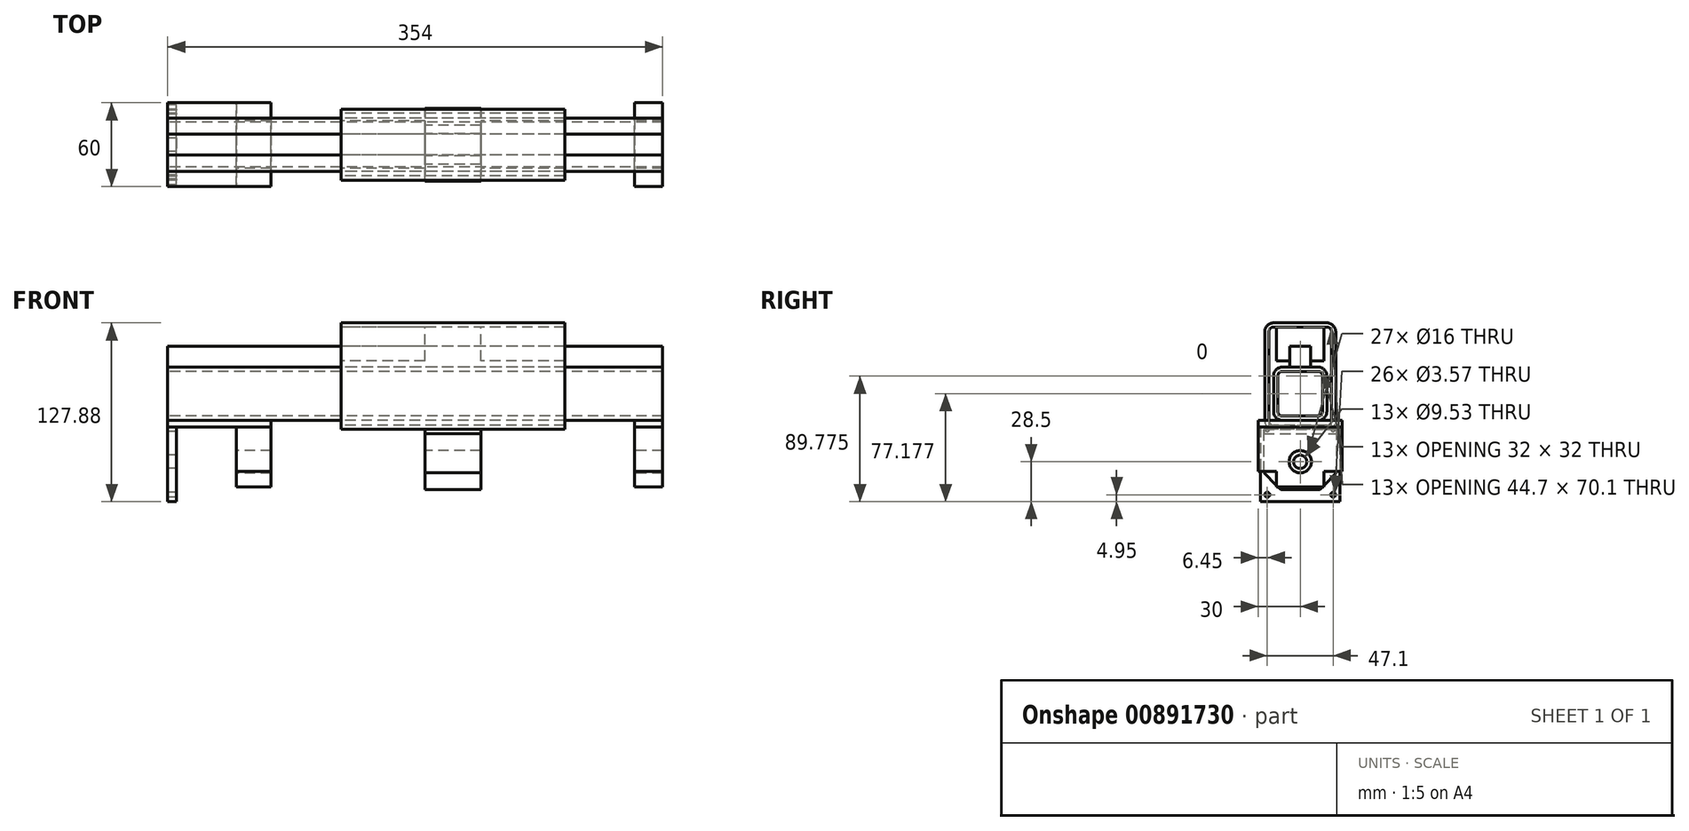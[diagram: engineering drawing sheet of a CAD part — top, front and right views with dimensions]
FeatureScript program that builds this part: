
annotation { "Feature Type Name" : "Feature", "Feature Type Description" : "" }
export const myFeature = defineFeature(function(context is Context, id is Id, definition is map)
    precondition{}
    {
        {
            var Q0;
            Q0=qCreatedBy(makeId("Right.planeOp"),FACE);
            var sketch = newSketch(context, id + "F0", { "sketchPlane" : qUnion([Q0])});
            skLineSegment(sketch, "E0", {"start": v(-26, 20) * mm, "end": v(26, 20) * mm});
            skLineSegment(sketch, "E1", {"start": v(26, 20) * mm, "end": v(26, -7.98) * mm});
            skLineSegment(sketch, "E2", {"start": v(26, -7.98) * mm, "end": v(13.98, -20) * mm});
            skLineSegment(sketch, "E3", {"start": v(13.98, -20) * mm, "end": v(-13.98, -20) * mm});
            skLineSegment(sketch, "E4", {"start": v(-13.98, -20) * mm, "end": v(-26, -7.98) * mm});
            skLineSegment(sketch, "E5", {"start": v(-26, -7.98) * mm, "end": v(-26, 20) * mm});
            skPoint(sketch, "E6", {"position": v(0, 0) * mm});
            skCircle(sketch, "E7", {"center": v(0, 0) * mm, "radius": 8 * mm});
            skSolve(sketch);
        }
        {
            var Q0;
            Q0=qCreatedBy(makeId("Right.planeOp"),FACE);
            var sketch = newSketch(context, id + "F1", { "sketchPlane" : qUnion([Q0])});
            skLineSegment(sketch, "E8.bottom", {"start": v(19.18, 96.33) * mm, "end": v(-19.18, 96.33) * mm});
            skLineSegment(sketch, "E8.top", {"start": v(19.18, 26.22) * mm, "end": v(-19.18, 26.22) * mm});
            skLineSegment(sketch, "E8.left", {"start": v(22.35, 93.15) * mm, "end": v(22.35, 29.4) * mm});
            skLineSegment(sketch, "E8.right", {"start": v(-22.35, 93.15) * mm, "end": v(-22.35, 29.4) * mm});
            skPoint(sketch, "E8.middle", {"position": v(0, 61.28) * mm});
            skLineSegment(sketch, "E9.bottom", {"start": v(19.05, 99.38) * mm, "end": v(-19.05, 99.38) * mm});
            skLineSegment(sketch, "E9.top", {"start": v(19.05, 23.18) * mm, "end": v(-19.05, 23.18) * mm});
            skLineSegment(sketch, "E9.left", {"start": v(25.4, 93.03) * mm, "end": v(25.4, 29.53) * mm});
            skLineSegment(sketch, "E9.right", {"start": v(-25.4, 93.03) * mm, "end": v(-25.4, 29.53) * mm});
            skPoint(sketch, "E10.visualSharp", {"position": v(-22.35, 96.33) * mm});
            skArc(sketch, "E10.filletArc", {"start": v(-19.18, 96.33) * mm, "mid": v(-21.42, 95.4) * mm, "end": v(-22.35, 93.15) * mm});
            skPoint(sketch, "E11.visualSharp", {"position": v(22.35, 96.33) * mm});
            skArc(sketch, "E11.filletArc", {"start": v(22.35, 93.15) * mm, "mid": v(21.42, 95.4) * mm, "end": v(19.18, 96.33) * mm});
            skPoint(sketch, "E12.visualSharp", {"position": v(22.35, 26.22) * mm});
            skArc(sketch, "E12.filletArc", {"start": v(19.18, 26.22) * mm, "mid": v(21.42, 27.15) * mm, "end": v(22.35, 29.4) * mm});
            skPoint(sketch, "E13.visualSharp", {"position": v(-22.35, 26.22) * mm});
            skArc(sketch, "E13.filletArc", {"start": v(-22.35, 29.4) * mm, "mid": v(-21.42, 27.15) * mm, "end": v(-19.18, 26.22) * mm});
            skPoint(sketch, "E14.visualSharp", {"position": v(-25.4, 99.38) * mm});
            skArc(sketch, "E14.filletArc", {"start": v(-19.05, 99.38) * mm, "mid": v(-23.54, 97.52) * mm, "end": v(-25.4, 93.03) * mm});
            skPoint(sketch, "E15.visualSharp", {"position": v(25.4, 99.38) * mm});
            skArc(sketch, "E15.filletArc", {"start": v(25.4, 93.03) * mm, "mid": v(23.54, 97.52) * mm, "end": v(19.05, 99.38) * mm});
            skPoint(sketch, "E16.visualSharp", {"position": v(25.4, 23.18) * mm});
            skArc(sketch, "E16.filletArc", {"start": v(19.05, 23.18) * mm, "mid": v(23.54, 25.03) * mm, "end": v(25.4, 29.53) * mm});
            skPoint(sketch, "E17.visualSharp", {"position": v(-25.4, 23.18) * mm});
            skArc(sketch, "E17.filletArc", {"start": v(-25.4, 29.53) * mm, "mid": v(-23.54, 25.03) * mm, "end": v(-19.05, 23.18) * mm});
            skLineSegment(sketch, "E18.bottom", {"start": v(-26, 23.18) * mm, "end": v(26, 23.18) * mm});
            skLineSegment(sketch, "E18.top", {"start": v(-26, 20) * mm, "end": v(26, 20) * mm});
            skLineSegment(sketch, "E18.left", {"start": v(-26, 23.18) * mm, "end": v(-26, 20) * mm});
            skLineSegment(sketch, "E18.right", {"start": v(26, 23.18) * mm, "end": v(26, 20) * mm});
            skSolve(sketch);
        }
        {
            var Q0;
            Q0=qCreatedBy(makeId("Right.planeOp"),FACE);
            var sketch = newSketch(context, id + "F2", { "sketchPlane" : qUnion([Q0])});
            skLineSegment(sketch, "E19.bottom", {"start": v(7.5, 67.73) * mm, "end": v(-7.5, 67.73) * mm});
            skLineSegment(sketch, "E19.top", {"start": v(7.5, 82.73) * mm, "end": v(-7.5, 82.73) * mm});
            skLineSegment(sketch, "E19.left", {"start": v(7.5, 67.73) * mm, "end": v(7.5, 82.73) * mm});
            skLineSegment(sketch, "E19.right", {"start": v(-7.5, 67.73) * mm, "end": v(-7.5, 82.73) * mm});
            skPoint(sketch, "E19.middle", {"position": v(0, 75.23) * mm});
            skLineSegment(sketch, "E20.bottom", {"start": v(17, 72.33) * mm, "end": v(-17, 72.33) * mm});
            skLineSegment(sketch, "E20.top", {"start": v(17, 96.33) * mm, "end": v(-17, 96.33) * mm});
            skLineSegment(sketch, "E20.left", {"start": v(17, 72.33) * mm, "end": v(17, 96.33) * mm});
            skLineSegment(sketch, "E20.right", {"start": v(-17, 72.33) * mm, "end": v(-17, 96.33) * mm});
            skPoint(sketch, "E20.middle", {"position": v(0, 84.33) * mm});
            skSolve(sketch);
        }
        {
            var Q0;
            Q0=qCreatedBy(makeId("Right.planeOp"),FACE);
            var sketch = newSketch(context, id + "F3", { "sketchPlane" : qUnion([Q0])});
            skLineSegment(sketch, "E21.bottom", {"start": v(12.83, 64.68) * mm, "end": v(-12.83, 64.68) * mm});
            skLineSegment(sketch, "E21.top", {"start": v(12.83, 32.67) * mm, "end": v(-12.83, 32.67) * mm});
            skLineSegment(sketch, "E21.left", {"start": v(16, 61.5) * mm, "end": v(16, 35.85) * mm});
            skLineSegment(sketch, "E21.right", {"start": v(-16, 61.5) * mm, "end": v(-16, 35.85) * mm});
            skPoint(sketch, "E21.middle", {"position": v(0, 48.68) * mm});
            skLineSegment(sketch, "E22.bottom", {"start": v(12.7, 67.73) * mm, "end": v(-12.7, 67.73) * mm});
            skLineSegment(sketch, "E22.top", {"start": v(12.7, 29.63) * mm, "end": v(-12.7, 29.63) * mm});
            skLineSegment(sketch, "E22.left", {"start": v(19.05, 61.38) * mm, "end": v(19.05, 35.98) * mm});
            skLineSegment(sketch, "E22.right", {"start": v(-19.05, 61.38) * mm, "end": v(-19.05, 35.98) * mm});
            skPoint(sketch, "E23.visualSharp", {"position": v(-16, 64.68) * mm});
            skArc(sketch, "E23.filletArc", {"start": v(-12.83, 64.68) * mm, "mid": v(-15.07, 63.75) * mm, "end": v(-16, 61.5) * mm});
            skPoint(sketch, "E24.visualSharp", {"position": v(16, 64.68) * mm});
            skArc(sketch, "E24.filletArc", {"start": v(16, 61.5) * mm, "mid": v(15.07, 63.75) * mm, "end": v(12.83, 64.68) * mm});
            skPoint(sketch, "E25.visualSharp", {"position": v(16, 32.67) * mm});
            skArc(sketch, "E25.filletArc", {"start": v(12.83, 32.67) * mm, "mid": v(15.07, 33.6) * mm, "end": v(16, 35.85) * mm});
            skPoint(sketch, "E26.visualSharp", {"position": v(-16, 32.67) * mm});
            skArc(sketch, "E26.filletArc", {"start": v(-16, 35.85) * mm, "mid": v(-15.07, 33.6) * mm, "end": v(-12.83, 32.67) * mm});
            skPoint(sketch, "E27.visualSharp", {"position": v(-19.05, 67.73) * mm});
            skArc(sketch, "E27.filletArc", {"start": v(-12.7, 67.73) * mm, "mid": v(-17.2, 65.87) * mm, "end": v(-19.05, 61.38) * mm});
            skPoint(sketch, "E28.visualSharp", {"position": v(19.05, 67.73) * mm});
            skArc(sketch, "E28.filletArc", {"start": v(19.05, 61.38) * mm, "mid": v(17.2, 65.87) * mm, "end": v(12.7, 67.73) * mm});
            skPoint(sketch, "E29.visualSharp", {"position": v(19.05, 29.63) * mm});
            skArc(sketch, "E29.filletArc", {"start": v(12.7, 29.63) * mm, "mid": v(17.2, 31.49) * mm, "end": v(19.05, 35.98) * mm});
            skPoint(sketch, "E30.visualSharp", {"position": v(-19.05, 29.63) * mm});
            skArc(sketch, "E30.filletArc", {"start": v(-19.05, 35.98) * mm, "mid": v(-17.2, 31.49) * mm, "end": v(-12.7, 29.63) * mm});
            skSolve(sketch);
        }
        {
            var Q0;
            Q0=qCreatedBy(makeId("Right.planeOp"),FACE);
            var sketch = newSketch(context, id + "F4", { "sketchPlane" : qUnion([Q0])});
            skLineSegment(sketch, "E31", {"start": v(-30, 25) * mm, "end": v(-30, -7) * mm});
            skLineSegment(sketch, "E32", {"start": v(-30, -7) * mm, "end": v(-17, -7) * mm});
            skLineSegment(sketch, "E33", {"start": v(-17, -7) * mm, "end": v(-17, -18) * mm});
            skLineSegment(sketch, "E34", {"start": v(-17, -18) * mm, "end": v(17, -18) * mm});
            skLineSegment(sketch, "E35", {"start": v(17, -18) * mm, "end": v(17, -7) * mm});
            skLineSegment(sketch, "E36", {"start": v(17, -7) * mm, "end": v(30, -7) * mm});
            skLineSegment(sketch, "E37", {"start": v(30, 25) * mm, "end": v(30, -7) * mm});
            skPoint(sketch, "E38", {"position": v(0, 0) * mm});
            skLineSegment(sketch, "E39", {"start": v(30, 25) * mm, "end": v(-30, 25) * mm});
            skCircle(sketch, "E40", {"center": v(0, 0) * mm, "radius": 8 * mm});
            skLineSegment(sketch, "E41.top", {"start": v(30, 29.63) * mm, "end": v(-30, 29.63) * mm});
            skLineSegment(sketch, "E41.left", {"start": v(30, 25) * mm, "end": v(30, 29.63) * mm});
            skLineSegment(sketch, "E41.right", {"start": v(-30, 25) * mm, "end": v(-30, 29.63) * mm});
            skPoint(sketch, "E41.middle", {"position": v(0, 27.31) * mm});
            skSolve(sketch);
        }
        {
            var Q0;
            Q0=qCreatedBy(makeId("Right.planeOp"),FACE);
            var sketch = newSketch(context, id + "F5", { "sketchPlane" : qUnion([Q0])});
            skLineSegment(sketch, "E42.bottom", {"start": v(23.55, -23.55) * mm, "end": v(-23.55, -23.55) * mm, "construction": true});
            skLineSegment(sketch, "E42.top", {"start": v(23.55, 23.55) * mm, "end": v(-23.55, 23.55) * mm, "construction": true});
            skLineSegment(sketch, "E42.left", {"start": v(23.55, -23.55) * mm, "end": v(23.55, 23.55) * mm, "construction": true});
            skLineSegment(sketch, "E42.right", {"start": v(-23.55, -23.55) * mm, "end": v(-23.55, 23.55) * mm, "construction": true});
            skCircle(sketch, "E43", {"center": v(-23.55, -23.55) * mm, "radius": 1.79 * mm});
            skCircle(sketch, "E44", {"center": v(-23.55, 23.55) * mm, "radius": 1.79 * mm});
            skCircle(sketch, "E45", {"center": v(23.55, 23.55) * mm, "radius": 1.79 * mm});
            skCircle(sketch, "E46", {"center": v(23.55, -23.55) * mm, "radius": 1.79 * mm});
            skPoint(sketch, "E47.middle", {"position": v(0, 0) * mm});
            skCircle(sketch, "E48", {"center": v(0, 0) * mm, "radius": 4.76 * mm});
            skLineSegment(sketch, "E49", {"start": v(23.55, 23.55) * mm, "end": v(-23.55, -23.55) * mm, "construction": true});
            skLineSegment(sketch, "E50.bottom", {"start": v(28.5, 28.5) * mm, "end": v(-28.5, 28.5) * mm, "construction": true});
            skLineSegment(sketch, "E50.top", {"start": v(28.5, -28.5) * mm, "end": v(-28.5, -28.5) * mm, "construction": true});
            skLineSegment(sketch, "E50.left", {"start": v(28.5, 28.5) * mm, "end": v(28.5, -28.5) * mm, "construction": true});
            skLineSegment(sketch, "E50.right", {"start": v(-28.5, 28.5) * mm, "end": v(-28.5, -28.5) * mm, "construction": true});
            skLineSegment(sketch, "E51.bottom", {"start": v(-28.5, 25) * mm, "end": v(28.5, 25) * mm});
            skLineSegment(sketch, "E51.top", {"start": v(-28.5, -28.5) * mm, "end": v(28.5, -28.5) * mm});
            skLineSegment(sketch, "E51.left", {"start": v(-28.5, 25) * mm, "end": v(-28.5, -28.5) * mm});
            skLineSegment(sketch, "E51.right", {"start": v(28.5, 25) * mm, "end": v(28.5, -28.5) * mm});
            skPoint(sketch, "E52", {"position": v(0, 31.35) * mm});
            skPoint(sketch, "E52.positionSnap0", {"position": v(0, 28.5) * mm});
            skSolve(sketch);
        }
        {
            var Q0;
            Q0=qCreatedBy(makeId("Front.planeOp"),FACE);
            var sketch = newSketch(context, id + "F6", { "sketchPlane" : qUnion([Q0])});
            skPoint(sketch, "E53", {"position": v(6.35, 0) * mm});
            skPoint(sketch, "E54", {"position": v(49, 0) * mm});
            skPoint(sketch, "E55", {"position": v(74, 0) * mm});
            skPoint(sketch, "E56", {"position": v(124, 0) * mm});
            skPoint(sketch, "E57", {"position": v(284, 0) * mm});
            skPoint(sketch, "E58", {"position": v(184, 0) * mm});
            skPoint(sketch, "E59", {"position": v(224, 0) * mm});
            skPoint(sketch, "E60", {"position": v(334, 0) * mm});
            skPoint(sketch, "E61", {"position": v(354, 0) * mm});
            skSolve(sketch);
        }
        {
            var Q0;
            Q0=makeQuery(id+"F5.imprint","IMPRINT",FACE,{"disambiguationData":[TD([[makeQuery(id+"F5.imprint","IMPRINT",EDGE,{"derivedFrom":sQuery(id+"F5.wireOp",EDGE,"E43")}),-1.0]])]});
            var Q1;
            Q1=sQuery(id+"F6.wireOp",VERTEX,"E53");
            extrude(context, id + "F7", {"entities" : qUnion([Q0]), "endBound" : BoundingType.UP_TO_VERTEX, "depth" : 25 * mm, "endBoundEntityVertex" : qUnion([Q1]), "offsetDistance" : 25 * mm});
        }
        {
            var Q0;
            {var subQ0=sQuery(id+"F4.wireOp",EDGE,"E31");Q0=makeQuery(id+"F4.imprint","IMPRINT",FACE,{"disambiguationData":[TD([[makeQuery(id+"F4.imprint","IMPRINT",EDGE,{"derivedFrom":subQ0}),1.0]])]});}
            var Q1;
            Q1=sQuery(id+"F6.wireOp",VERTEX,"E55");
            var Q2;
            Q2=sQuery(id+"F6.wireOp",VERTEX,"E54");
            extrude(context, id + "F8", {"entities" : qUnion([Q0]), "endBound" : BoundingType.UP_TO_VERTEX, "depth" : 25 * mm, "endBoundEntityVertex" : qUnion([Q1]), "offsetDistance" : 25 * mm, "hasSecondDirection" : true, "secondDirectionBound" : BoundingType.UP_TO_VERTEX, "secondDirectionOppositeDirection" : false, "secondDirectionDepth" : 25 * mm, "secondDirectionBoundEntityVertex" : qUnion([Q2])});
        }
        {
            var Q0;
            Q0=makeQuery(id+"F1.imprint","IMPRINT",FACE,{"disambiguationData":[TD([[makeQuery(id+"F1.imprint","IMPRINT",EDGE,{"derivedFrom":sQuery(id+"F1.wireOp",EDGE,"E8.bottom")}),-1.0]])]});
            var Q1;
            Q1=sQuery(id+"F6.wireOp",VERTEX,"E57");
            var Q2;
            Q2=sQuery(id+"F6.wireOp",VERTEX,"E56");
            extrude(context, id + "F9", {"entities" : qUnion([Q0]), "endBound" : BoundingType.UP_TO_VERTEX, "depth" : 25 * mm, "endBoundEntityVertex" : qUnion([Q1]), "offsetDistance" : 25 * mm, "hasSecondDirection" : true, "secondDirectionBound" : BoundingType.UP_TO_VERTEX, "secondDirectionOppositeDirection" : false, "secondDirectionDepth" : 25 * mm, "secondDirectionBoundEntityVertex" : qUnion([Q2])});
        }
        {
            var Q0;
            Q0=makeQuery(id+"F3.imprint","IMPRINT",FACE,{"disambiguationData":[TD([[makeQuery(id+"F3.imprint","IMPRINT",EDGE,{"derivedFrom":sQuery(id+"F3.wireOp",EDGE,"E21.bottom")}),-1.0]])]});
            var Q1;
            Q1=sQuery(id+"F6.wireOp",VERTEX,"E61");
            extrude(context, id + "F10", {"entities" : qUnion([Q0]), "endBound" : BoundingType.UP_TO_VERTEX, "depth" : 25 * mm, "endBoundEntityVertex" : qUnion([Q1]), "offsetDistance" : 25 * mm});
        }
        {
            var Q0;
            Q0=makeQuery(id+"F0.imprint","IMPRINT",FACE,{"disambiguationData":[TD([[makeQuery(id+"F0.imprint","IMPRINT",EDGE,{"derivedFrom":sQuery(id+"F0.wireOp",EDGE,"E0")}),-1.0]])]});
            var Q1;
            Q1=sQuery(id+"F6.wireOp",VERTEX,"E59");
            var Q2;
            Q2=sQuery(id+"F6.wireOp",VERTEX,"E58");
            extrude(context, id + "F11", {"entities" : qUnion([Q0]), "operationType" : NewBodyOperationType.ADD, "endBound" : BoundingType.UP_TO_VERTEX, "depth" : 25 * mm, "endBoundEntityVertex" : qUnion([Q1]), "offsetDistance" : 25 * mm, "hasSecondDirection" : true, "secondDirectionBound" : BoundingType.UP_TO_VERTEX, "secondDirectionOppositeDirection" : false, "secondDirectionDepth" : 25 * mm, "secondDirectionBoundEntityVertex" : qUnion([Q2])});
        }
        {
            var Q0;
            Q0=makeQuery(id+"F4.imprint","IMPRINT",FACE,{"disambiguationData":[TD([[makeQuery(id+"F4.imprint","IMPRINT",EDGE,{"derivedFrom":sQuery(id+"F4.wireOp",EDGE,"E41.top")}),1.0]])]});
            var Q1;
            Q1=sQuery(id+"F6.wireOp",VERTEX,"E55");
            extrude(context, id + "F12", {"entities" : qUnion([Q0]), "endBound" : BoundingType.UP_TO_VERTEX, "depth" : 25 * mm, "endBoundEntityVertex" : qUnion([Q1]), "offsetDistance" : 25 * mm});
        }
        {
            var Q0;
            {var subQ0=sQuery(id+"F4.wireOp",EDGE,"E31");Q0=makeQuery(id+"F4.imprint","IMPRINT",FACE,{"disambiguationData":[TD([[makeQuery(id+"F4.imprint","IMPRINT",EDGE,{"derivedFrom":subQ0}),1.0]])]});}
            var Q1;
            Q1=sQuery(id+"F6.wireOp",VERTEX,"E61");
            var Q2;
            Q2=sQuery(id+"F6.wireOp",VERTEX,"E60");
            extrude(context, id + "F13", {"entities" : qUnion([Q0]), "endBound" : BoundingType.UP_TO_VERTEX, "depth" : 25 * mm, "endBoundEntityVertex" : qUnion([Q1]), "offsetDistance" : 25 * mm, "hasSecondDirection" : true, "secondDirectionBound" : BoundingType.UP_TO_VERTEX, "secondDirectionOppositeDirection" : false, "secondDirectionDepth" : 25 * mm, "secondDirectionBoundEntityVertex" : qUnion([Q2])});
        }
        {
            var Q0;
            Q0=makeQuery(id+"F4.imprint","IMPRINT",FACE,{"disambiguationData":[TD([[makeQuery(id+"F4.imprint","IMPRINT",EDGE,{"derivedFrom":sQuery(id+"F4.wireOp",EDGE,"E41.top")}),1.0]])]});
            var Q1;
            Q1=sQuery(id+"F6.wireOp",VERTEX,"E61");
            var Q2;
            Q2=sQuery(id+"F6.wireOp",VERTEX,"E60");
            extrude(context, id + "F14", {"entities" : qUnion([Q0]), "endBound" : BoundingType.UP_TO_VERTEX, "depth" : 25 * mm, "endBoundEntityVertex" : qUnion([Q1]), "offsetDistance" : 25 * mm, "hasSecondDirection" : true, "secondDirectionBound" : BoundingType.UP_TO_VERTEX, "secondDirectionOppositeDirection" : false, "secondDirectionDepth" : 25 * mm, "secondDirectionBoundEntityVertex" : qUnion([Q2])});
        }
        {
            var Q0;
            {var subQ1=sQuery(id+"F1.wireOp",EDGE,"E9.top");Q0=makeQuery(id+"F1.imprint","IMPRINT",FACE,{"disambiguationData":[TD([[makeQuery(id+"F1.imprint","IMPRINT",EDGE,{"derivedFrom":subQ1}),1.0]])]});}
            var Q1;
            Q1=sQuery(id+"F6.wireOp",VERTEX,"E59");
            var Q2;
            Q2=sQuery(id+"F6.wireOp",VERTEX,"E58");
            extrude(context, id + "F15", {"entities" : qUnion([Q0]), "endBound" : BoundingType.UP_TO_VERTEX, "depth" : 25 * mm, "endBoundEntityVertex" : qUnion([Q1]), "offsetDistance" : 25 * mm, "hasSecondDirection" : true, "secondDirectionBound" : BoundingType.UP_TO_VERTEX, "secondDirectionOppositeDirection" : false, "secondDirectionDepth" : 25 * mm, "secondDirectionBoundEntityVertex" : qUnion([Q2])});
        }
        {
            var Q0;
            {var subQ0=sQuery(id+"F2.wireOp",EDGE,"E19.top");Q0=makeQuery(id+"F2.imprint","IMPRINT",FACE,{"disambiguationData":[TD([[makeQuery(id+"F2.imprint","IMPRINT",EDGE,{"derivedFrom":subQ0}),1.0]])]});}
            var Q1;
            {var subQ0=sQuery(id+"F2.wireOp",EDGE,"E19.bottom");Q1=makeQuery(id+"F2.imprint","IMPRINT",FACE,{"disambiguationData":[TD([[makeQuery(id+"F2.imprint","IMPRINT",EDGE,{"derivedFrom":subQ0}),-1.0]])]});}
            var Q2;
            Q2=sQuery(id+"F6.wireOp",VERTEX,"E61");
            extrude(context, id + "F16", {"entities" : qUnion([Q0, Q1]), "endBound" : BoundingType.UP_TO_VERTEX, "depth" : 25 * mm, "endBoundEntityVertex" : qUnion([Q2]), "offsetDistance" : 25 * mm});
        }
        {
            var Q0;
            {var subQ1=sQuery(id+"F2.wireOp",EDGE,"E19.top");Q0=makeQuery(id+"F2.imprint","IMPRINT",FACE,{"disambiguationData":[TD([[makeQuery(id+"F2.imprint","IMPRINT",EDGE,{"derivedFrom":subQ1}),-1.0]])]});}
            var Q1;
            Q1=sQuery(id+"F6.wireOp",VERTEX,"E58");
            var Q2;
            Q2=sQuery(id+"F6.wireOp",VERTEX,"E56");
            extrude(context, id + "F17", {"entities" : qUnion([Q0]), "endBound" : BoundingType.UP_TO_VERTEX, "depth" : 25 * mm, "endBoundEntityVertex" : qUnion([Q1]), "offsetDistance" : 25 * mm, "hasSecondDirection" : true, "secondDirectionBound" : BoundingType.UP_TO_VERTEX, "secondDirectionOppositeDirection" : false, "secondDirectionDepth" : 25 * mm, "secondDirectionBoundEntityVertex" : qUnion([Q2])});
        }
        {
            var Q0;
            {var subQ1=sQuery(id+"F2.wireOp",EDGE,"E19.top");Q0=makeQuery(id+"F2.imprint","IMPRINT",FACE,{"disambiguationData":[TD([[makeQuery(id+"F2.imprint","IMPRINT",EDGE,{"derivedFrom":subQ1}),-1.0]])]});}
            var Q1;
            Q1=sQuery(id+"F6.wireOp",VERTEX,"E57");
            var Q2;
            Q2=sQuery(id+"F6.wireOp",VERTEX,"E59");
            extrude(context, id + "F18", {"entities" : qUnion([Q0]), "endBound" : BoundingType.UP_TO_VERTEX, "depth" : 25 * mm, "endBoundEntityVertex" : qUnion([Q1]), "offsetDistance" : 25 * mm, "hasSecondDirection" : true, "secondDirectionBound" : BoundingType.UP_TO_VERTEX, "secondDirectionOppositeDirection" : false, "secondDirectionDepth" : 25 * mm, "secondDirectionBoundEntityVertex" : qUnion([Q2])});
        }
    });
